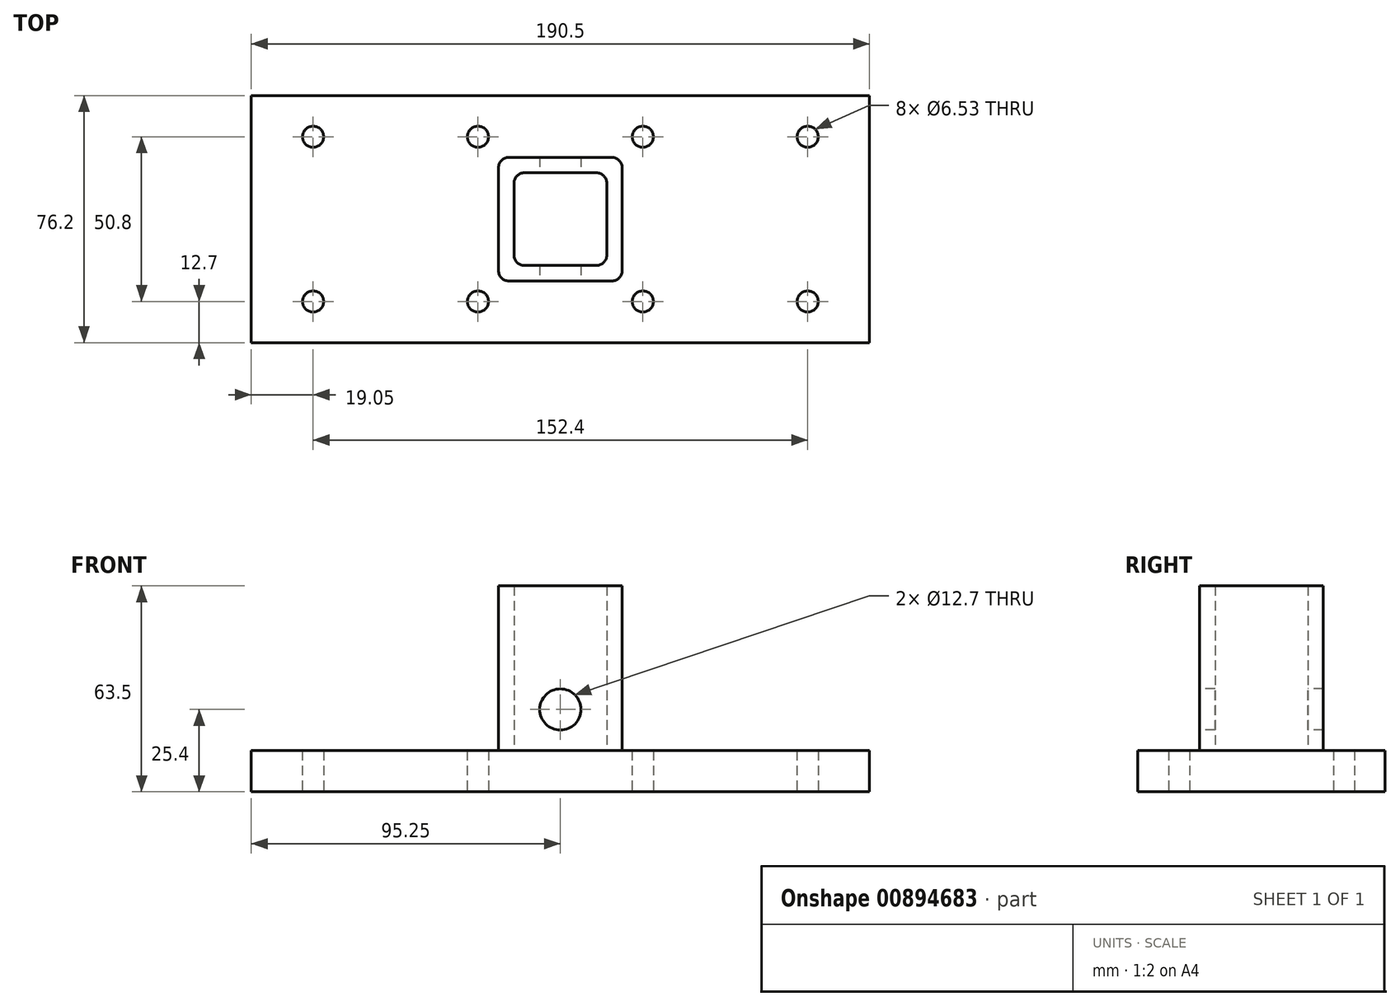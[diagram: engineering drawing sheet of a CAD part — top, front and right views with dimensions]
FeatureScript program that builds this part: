
annotation { "Feature Type Name" : "Feature", "Feature Type Description" : "" }
export const myFeature = defineFeature(function(context is Context, id is Id, definition is map)
    precondition{}
    {
        {
            var Q0;
            Q0=qCreatedBy(makeId("Top.planeOp"),FACE);
            var sketch = newSketch(context, id + "F0", { "sketchPlane" : qUnion([Q0])});
            skLineSegment(sketch, "E0.bottom", {"start": v(95.25, 38.1) * mm, "end": v(-95.25, 38.1) * mm});
            skLineSegment(sketch, "E0.top", {"start": v(95.25, -38.1) * mm, "end": v(-95.25, -38.1) * mm});
            skLineSegment(sketch, "E0.left", {"start": v(95.25, 38.1) * mm, "end": v(95.25, -38.1) * mm});
            skLineSegment(sketch, "E0.right", {"start": v(-95.25, 38.1) * mm, "end": v(-95.25, -38.1) * mm});
            skPoint(sketch, "E0.middle", {"position": v(0, 0) * mm});
            skSolve(sketch);
        }
        {
            var Q0;
            Q0 = qSketchRegion(id + "F0", true);
            extrude(context, id + "F1", {"entities" : qUnion([Q0]), "endBound" : BoundingType.SYMMETRIC, "depth" : 12.7 * mm, "offsetDistance" : 25.4 * mm});
        }
        {
            var Q0;
            Q0=makeQuery(id+"F1.opExtrude","CAP_FACE",FACE,{"disambiguationData":[OSD([sQuery(id+"F0.wireOp",EDGE,"E0.bottom"),sQuery(id+"F0.wireOp",EDGE,"E0.top"),sQuery(id+"F0.wireOp",EDGE,"E0.left"),sQuery(id+"F0.wireOp",EDGE,"E0.right")])],"isStart":true});
            var sketch = newSketch(context, id + "F2", { "sketchPlane" : qUnion([Q0])});
            skPoint(sketch, "E1", {"position": v(-76.2, 25.4) * mm});
            skPoint(sketch, "E2", {"position": v(76.2, 25.4) * mm});
            skPoint(sketch, "E3", {"position": v(76.2, -25.4) * mm});
            skPoint(sketch, "E4", {"position": v(-76.2, -25.4) * mm});
            skPoint(sketch, "E5", {"position": v(-25.4, -25.4) * mm});
            skPoint(sketch, "E6", {"position": v(25.4, -25.4) * mm});
            skPoint(sketch, "E7", {"position": v(-25.4, 25.4) * mm});
            skPoint(sketch, "E8", {"position": v(25.4, 25.4) * mm});
            skSolve(sketch);
        }
        {
            var Q0;
            Q0=sQuery(id+"F2.wireOp",VERTEX,"E4");
            var Q1;
            Q1=sQuery(id+"F2.wireOp",VERTEX,"E5");
            var Q2;
            Q2=sQuery(id+"F2.wireOp",VERTEX,"E1");
            var Q3;
            Q3=sQuery(id+"F2.wireOp",VERTEX,"E7");
            var Q4;
            Q4=sQuery(id+"F2.wireOp",VERTEX,"E8");
            var Q5;
            Q5=sQuery(id+"F2.wireOp",VERTEX,"E6");
            var Q6;
            Q6=sQuery(id+"F2.wireOp",VERTEX,"E3");
            var Q7;
            Q7=sQuery(id+"F2.wireOp",VERTEX,"E2");
            var Q8;
            Q8=sQuery(id+"F2.wireOp",VERTEX,"2436656a-3f81-4026-997d-c2f7a2f26986");
            var Q9;
            Q9=sQuery(id+"F2.wireOp",VERTEX,"169edbf6-3af3-45d2-9528-35a83c8f3200");
            var Q10;
            Q10=makeQuery(id+"F1.opExtrude","SWEPT_BODY",BODY,{"disambiguationData":[OSD([sQuery(id+"F0.wireOp",EDGE,"E0.bottom"),sQuery(id+"F0.wireOp",EDGE,"E0.top"),sQuery(id+"F0.wireOp",EDGE,"E0.left"),sQuery(id+"F0.wireOp",EDGE,"E0.right")])]});
            hole(context, id + "F3", {"style" : HoleStyle.SIMPLE, "endStyle" : HoleEndStyle.THROUGH, "standardTappedOrClearance" : lookupTablePath({ "standard" : "ANSI", "engagement" : "75%", "pitch" : "18 tpi", "size" : "5/16", "type" : "Tapped" }), "standardBlindInLast" : lookupTablePath({ "standard" : "ANSI", "engagement" : "75%", "pitch" : "18 tpi", "size" : "5/16", "type" : "Tapped" }), "holeDiameter" : 6.53 * mm, "majorDiameter" : 7.94 * mm, "showTappedDepth" : true, "isTappedThrough" : true, "tappedDepth" : 12.7 * mm, "tapClearance" : 3, "startFromSketch" : true, "locations" : qUnion([Q0, Q1, Q2, Q3, Q4, Q5, Q6, Q7, Q8, Q9]), "scope" : qUnion([Q10])});
        }
        {
            var Q0;
            Q0=makeQuery(id+"F1.opExtrude","CAP_FACE",FACE,{"disambiguationData":[OSD([sQuery(id+"F0.wireOp",EDGE,"E0.bottom"),sQuery(id+"F0.wireOp",EDGE,"E0.top"),sQuery(id+"F0.wireOp",EDGE,"E0.left"),sQuery(id+"F0.wireOp",EDGE,"E0.right")])],"isStart":false});
            var sketch = newSketch(context, id + "F4", { "sketchPlane" : qUnion([Q0])});
            skLineSegment(sketch, "E9.bottom", {"start": v(19.05, 19.05) * mm, "end": v(-19.05, 19.05) * mm});
            skLineSegment(sketch, "E9.top", {"start": v(19.05, -19.05) * mm, "end": v(-19.05, -19.05) * mm});
            skLineSegment(sketch, "E9.left", {"start": v(19.05, 19.05) * mm, "end": v(19.05, -19.05) * mm});
            skLineSegment(sketch, "E9.right", {"start": v(-19.05, 19.05) * mm, "end": v(-19.05, -19.05) * mm});
            skPoint(sketch, "E9.middle", {"position": v(0, 0) * mm});
            skLineSegment(sketch, "E10.bottom", {"start": v(14.29, 14.29) * mm, "end": v(-14.29, 14.29) * mm});
            skLineSegment(sketch, "E10.top", {"start": v(14.29, -14.29) * mm, "end": v(-14.29, -14.29) * mm});
            skLineSegment(sketch, "E10.left", {"start": v(14.29, 14.29) * mm, "end": v(14.29, -14.29) * mm});
            skLineSegment(sketch, "E10.right", {"start": v(-14.29, 14.29) * mm, "end": v(-14.29, -14.29) * mm});
            skSolve(sketch);
        }
        {
            var Q0;
            Q0 = qSketchRegion(id + "F4", true);
            extrude(context, id + "F5", {"entities" : qUnion([Q0]), "operationType" : NewBodyOperationType.ADD, "depth" : 50.8 * mm, "offsetDistance" : 25.4 * mm});
        }
        {
            var Q0;
            Q0=makeQuery(id+"F5.opExtrude","SWEPT_EDGE",EDGE,{"disambiguationData":[OSD([sQuery(id+"F4.wireOp",EDGE,"E9.top"),sQuery(id+"F4.wireOp",EDGE,"E9.right")])]});
            var Q1;
            Q1=makeQuery(id+"F5.opExtrude","SWEPT_EDGE",EDGE,{"disambiguationData":[OSD([sQuery(id+"F4.wireOp",EDGE,"E9.top"),sQuery(id+"F4.wireOp",EDGE,"E9.left")])]});
            var Q2;
            Q2=makeQuery(id+"F5.opExtrude","SWEPT_EDGE",EDGE,{"disambiguationData":[OSD([sQuery(id+"F4.wireOp",EDGE,"E10.bottom"),sQuery(id+"F4.wireOp",EDGE,"E10.right")])]});
            var Q3;
            Q3=makeQuery(id+"F5.opExtrude","SWEPT_EDGE",EDGE,{"disambiguationData":[OSD([sQuery(id+"F4.wireOp",EDGE,"E10.bottom"),sQuery(id+"F4.wireOp",EDGE,"E10.left")])]});
            var Q4;
            Q4=makeQuery(id+"F5.opExtrude","SWEPT_EDGE",EDGE,{"disambiguationData":[OSD([sQuery(id+"F4.wireOp",EDGE,"E10.top"),sQuery(id+"F4.wireOp",EDGE,"E10.right")])]});
            var Q5;
            Q5=makeQuery(id+"F5.opExtrude","SWEPT_EDGE",EDGE,{"disambiguationData":[OSD([sQuery(id+"F4.wireOp",EDGE,"E10.top"),sQuery(id+"F4.wireOp",EDGE,"E10.left")])]});
            var Q6;
            Q6=makeQuery(id+"F5.opExtrude","SWEPT_EDGE",EDGE,{"disambiguationData":[OSD([sQuery(id+"F4.wireOp",EDGE,"E9.bottom"),sQuery(id+"F4.wireOp",EDGE,"E9.right")])]});
            var Q7;
            Q7=makeQuery(id+"F5.opExtrude","SWEPT_EDGE",EDGE,{"disambiguationData":[OSD([sQuery(id+"F4.wireOp",EDGE,"E9.bottom"),sQuery(id+"F4.wireOp",EDGE,"E9.left")])]});
            fillet(context, id + "F6", {"entities" : qUnion([Q0, Q1, Q2, Q3, Q4, Q5, Q6, Q7]), "radius" : 3.17 * mm, "tangentPropagation" : true, "allowEdgeOverflow" : false});
        }
        {
            var Q0;
            Q0=makeQuery(id+"F5.opExtrude","SWEPT_FACE",FACE,{"disambiguationData":[OSD([sQuery(id+"F4.wireOp",EDGE,"E9.top")])]});
            var sketch = newSketch(context, id + "F7", { "sketchPlane" : qUnion([Q0])});
            skCircle(sketch, "E11", {"center": v(0, 19.05) * mm, "radius": 6.35 * mm});
            skSolve(sketch);
        }
        {
            var Q0;
            Q0 = qSketchRegion(id + "F7", true);
            var Q1;
            Q1=makeQuery(id+"F5.opExtrude","SWEPT_FACE",FACE,{"disambiguationData":[OSD([sQuery(id+"F4.wireOp",EDGE,"E9.bottom")])]});
            extrude(context, id + "F8", {"entities" : qUnion([Q0]), "operationType" : NewBodyOperationType.REMOVE, "endBound" : BoundingType.UP_TO_SURFACE, "oppositeDirection" : true, "depth" : 25.4 * mm, "endBoundEntityFace" : qUnion([Q1]), "offsetDistance" : 25.4 * mm});
        }
    });
